# Revit family: Skylight-Wasco-Pyramid_System
name_source: partatom
category: Windows
revit_build: Autodesk Revit Architecture 2013 (Build: 20130531_2115(x64)
units: mm (PartAtom-declared; Revit-internal decimal feet)

## types (9) — shared parameters
Curb = Wood - Wasco - Douglas Firs
Curb Height = 0' - 3 1/32"
Default Elevation = 4' - 0"
Description = Skylight
Finish = Aluminum - Wasco - Aged Copper
Glazing 1 5_16 = No
Glazing Material = Glass - Wasco - Clear
Manufacturer = Wasco
Product Documentation Link = http://www.wascoskylights.com
Product Name = Pyramid
Product Page URL = http://www.wascoskylights.com
Sill Height Offset = 0' - 0 17/32"
Sill Width Offset = 0' - 5 31/32"
URL = http://www.wascoskylights.com

## per-type parameters (varying)
- Pinnacle 350 - 5/12: Angle=22.62°; Angle C=157.38°; C Masking Region Depth=0' - 6 23/32"; C Pyramid Width=11' - 4 13/32"; Curb Width=0' - 4"; Glazing Area=16.13 SF; Glazing Thickness=0' - 1 1/16"; Height=2' - 10 5/16"; Host Width=13' - 0"; Hypotenuse=6' - 2 1/32"; Model=Pinnacle 350; Pinnacle=Base Plate - Sill : 350; Pinnacle 350=Yes; Pinnacle 600=No; Pinnacle 900=No; Pitch=5; Pitch 12 12=No; Pitch 5 12=Yes; Pitch 7 12=No; Pitch Actual=5; Purlin=No; Pyramid Height=2' - 4 15/32"; Pyramid Height Offset=0' - 5 5/16"; Pyramid Width=11' - 4 21/32"; Pyramid Width Offset=0' - 2 7/32"; Rafter Depth=0' - 5"; Rough Height=3' - 1 11/32"; Rough Width=11' - 4 21/32"; Width=11' - 0"; Width Actual=11' - 0"
- Pinnacle 600 - 5/12: Angle=22.62°; Angle C=157.38°; C Masking Region Depth=0' - 7 21/32"; C Pyramid Width=20' - 6 11/32"; Curb Width=0' - 4"; Glazing Area=54.57 SF; Glazing Thickness=0' - 1 3/16"; Height=4' - 11 17/32"; Host Width=22' - 0"; Hypotenuse=11' - 1 9/16"; Model=Pinnacle 600; Pinnacle=Base Plate - Sill : 600; Pinnacle 350=No; Pinnacle 600=Yes; Pinnacle 900=No; Pitch=5; Pitch 12 12=No; Pitch 5 12=Yes; Pitch 7 12=No; Pitch Actual=5; Purlin=No; Pyramid Height=4' - 3 3/8"; Pyramid Height Offset=0' - 7 5/8"; Pyramid Width=20' - 6 19/32"; Pyramid Width Offset=0' - 3 5/32"; Rafter Depth=0' - 7 7/8"; Rough Height=5' - 2 9/16"; Rough Width=20' - 6 19/32"; Width=20' - 0"; Width Actual=20' - 0"
- Pinnacle 900 - 5/12: Angle=22.62°; Angle C=157.38°; C Masking Region Depth=0' - 10 11/16"; C Pyramid Width=28' - 8 13/32"; Curb Width=0' - 6"; Glazing Area=109.16 SF; Glazing Thickness=0' - 1 3/16"; Height=6' - 10 25/32"; Host Width=30' - 0"; Hypotenuse=15' - 7 5/8"; Model=Pinnacle 900; Pinnacle=Base Plate - Sill : 900; Pinnacle 350=No; Pinnacle 600=No; Pinnacle 900=Yes; Pitch=5; Pitch 12 12=No; Pitch 5 12=Yes; Pitch 7 12=No; Pitch Actual=5; Purlin=No; Pyramid Height=6' - 0 5/32"; Pyramid Height Offset=0' - 10 1/16"; Pyramid Width=28' - 10 13/32"; Pyramid Width Offset=0' - 4 3/16"; Rafter Depth=0' - 10 3/4"; Rough Height=7' - 1 13/16"; Rough Width=28' - 10 13/32"; Width=28' - 0"; Width Actual=28' - 0"
- Pinnacle 350 - 7/12: Angle=30.26°; Angle C=149.74°; C Masking Region Depth=0' - 7 13/32"; C Pyramid Width=10' - 5 13/16"; Curb Width=0' - 4"; Glazing Area=14.6 SF; Glazing Thickness=0' - 1 1/16"; Height=3' - 6 9/32"; Host Width=12' - 0"; Hypotenuse=6' - 0 31/32"; Model=Pinnacle 350; Pinnacle=Base Plate - Sill : 350; Pinnacle 350=Yes; Pinnacle 600=No; Pinnacle 900=No; Pitch=7; Pitch 12 12=No; Pitch 5 12=No; Pitch 7 12=Yes; Pitch Actual=7; Purlin=No; Pyramid Height=3' - 0 3/4"; Pyramid Height Offset=0' - 4 31/32"; Pyramid Width=10' - 6 1/16"; Pyramid Width Offset=0' - 2 29/32"; Rafter Depth=0' - 5"; Rough Height=3' - 9 5/16"; Rough Width=10' - 6 1/16"; Width=10' - 0"; Width Actual=10' - 0"
- Pinnacle 350 - 12/12: Angle=45.00°; Angle C=135.00°; C Masking Region Depth=0' - 8 5/8"; C Pyramid Width=9' - 8 1/4"; Curb Width=0' - 4"; Glazing Area=15.23 SF; Glazing Thickness=0' - 1 1/16"; Height=5' - 2 29/32"; Host Width=11' - 0"; Hypotenuse=6' - 10 3/8"; Model=Pinnacle 350; Pinnacle=Base Plate - Sill : 350; Pinnacle 350=Yes; Pinnacle 600=No; Pinnacle 900=No; Pitch=12; Pitch 12 12=Yes; Pitch 5 12=No; Pitch 7 12=No; Pitch Actual=12; Purlin=No; Pyramid Height=4' - 10 1/4"; Pyramid Height Offset=0' - 4 1/8"; Pyramid Width=9' - 8 1/2"; Pyramid Width Offset=0' - 4 1/8"; Rafter Depth=0' - 5"; Rough Height=5' - 5 15/16"; Rough Width=9' - 8 1/2"; Width=9' - 0"; Width Actual=9' - 0"
- Pinnacle 600 - 7/12: Angle=30.26°; Angle C=149.74°; C Masking Region Depth=0' - 8 21/32"; C Pyramid Width=19' - 8 5/16"; Curb Width=0' - 4"; Glazing Area=53.64 SF; Glazing Thickness=0' - 1 3/16"; Height=6' - 4 21/32"; Host Width=21' - 0"; Hypotenuse=11' - 4 15/16"; Model=Pinnacle 600; Pinnacle=Base Plate - Sill : 600; Pinnacle 350=No; Pinnacle 600=Yes; Pinnacle 900=No; Pitch=7; Pitch 12 12=No; Pitch 5 12=No; Pitch 7 12=Yes; Pitch Actual=7; Purlin=No; Pyramid Height=5' - 9"; Pyramid Height Offset=0' - 7 1/8"; Pyramid Width=19' - 8 9/16"; Pyramid Width Offset=0' - 4 5/32"; Rafter Depth=0' - 7 7/8"; Rough Height=6' - 7 11/16"; Rough Width=19' - 8 9/16"; Width=19' - 0"; Width Actual=19' - 0"
- Pinnacle 600 - 12/12: Angle=45.00°; Angle C=135.00°; C Masking Region Depth=0' - 10 13/32"; C Pyramid Width=15' - 11 25/32"; Curb Width=0' - 4"; Glazing Area=42.9 SF; Glazing Thickness=0' - 1 3/16"; Height=8' - 6 15/32"; Host Width=17' - 0"; Hypotenuse=11' - 3 25/32"; Model=Pinnacle 600; Pinnacle=Base Plate - Sill : 600; Pinnacle 350=No; Pinnacle 600=Yes; Pinnacle 900=No; Pitch=12; Pitch 12 12=Yes; Pitch 5 12=No; Pitch 7 12=No; Pitch Actual=12; Purlin=No; Pyramid Height=8' - 0 1/32"; Pyramid Height Offset=0' - 5 29/32"; Pyramid Width=16' - 0 1/32"; Pyramid Width Offset=0' - 5 29/32"; Rafter Depth=0' - 7 7/8"; Rough Height=8' - 9 1/2"; Rough Width=16' - 0 1/32"; Width=15' - 0"; Width Actual=15' - 0"
- Pinnacle 900 - 7/12: Angle=30.26°; Angle C=149.74°; C Masking Region Depth=0' - 11 31/32"; C Pyramid Width=27' - 4 29/32"; Curb Width=0' - 6"; Glazing Area=106.4 SF; Glazing Thickness=0' - 1 3/16"; Height=8' - 10 13/32"; Host Width=28' - 6"; Hypotenuse=15' - 11 9/16"; Model=Pinnacle 900; Pinnacle=Base Plate - Sill : 900; Pinnacle 350=No; Pinnacle 600=No; Pinnacle 900=Yes; Pitch=7; Pitch 12 12=No; Pitch 5 12=No; Pitch 7 12=Yes; Pitch Actual=7; Purlin=Yes; Pyramid Height=8' - 0 17/32"; Pyramid Height Offset=0' - 9 11/32"; Pyramid Width=27' - 6 29/32"; Pyramid Width Offset=0' - 5 15/32"; Rafter Depth=0' - 10 3/4"; Rough Height=9' - 1 7/16"; Rough Width=27' - 6 29/32"; Width=26' - 6"; Width Actual=26' - 6"
- Pinnacle 900 - 12/12: Angle=45.00°; Angle C=135.00°; C Masking Region Depth=1' - 2 1/32"; C Pyramid Width=23' - 3 3/32"; Curb Width=0' - 6"; Glazing Area=93.5 SF; Glazing Thickness=0' - 1 3/16"; Height=12' - 4 5/8"; Host Width=24' - 0"; Hypotenuse=16' - 6 3/4"; Model=Pinnacle 900; Pinnacle=Base Plate - Sill : 900; Pinnacle 350=No; Pinnacle 600=No; Pinnacle 900=Yes; Pitch=14; Pitch 12 12=Yes; Pitch 5 12=No; Pitch 7 12=No; Pitch Actual=12; Purlin=Yes; Pyramid Height=11' - 8 17/32"; Pyramid Height Offset=0' - 7 17/32"; Pyramid Width=23' - 5 3/32"; Pyramid Width Offset=0' - 7 17/32"; Rafter Depth=0' - 10 3/4"; Rough Height=12' - 7 21/32"; Rough Width=23' - 5 3/32"; Width=22' - 0"; Width Actual=22' - 0"

## geometry (parser evidence)
native form markers: Blend x20, Sweep x13
no freeform markers — native parametric forms only
